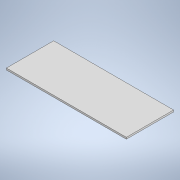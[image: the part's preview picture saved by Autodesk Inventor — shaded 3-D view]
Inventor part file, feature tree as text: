
AUTODESK INVENTOR PART (.ipt)
format: ipt  version: 2021 (Build 250183000, 183)  size: 92,672 bytes
history: native  units: mm
features: extrude x1, sketch x1
ambient origin geometry x8: Origin, YZ Plane, XZ Plane, XY Plane, X Axis, Y Axis, Z Axis, Center Point
bodies: Solid1 (feature_tree)
feature tree (2):
  extrude  "Extrusion1"  Depth=137.0mm
  sketch  "Sketch1"  dims[d0=348.0mm d1=137.0mm d2=5.0mm d3=0.0mm]
